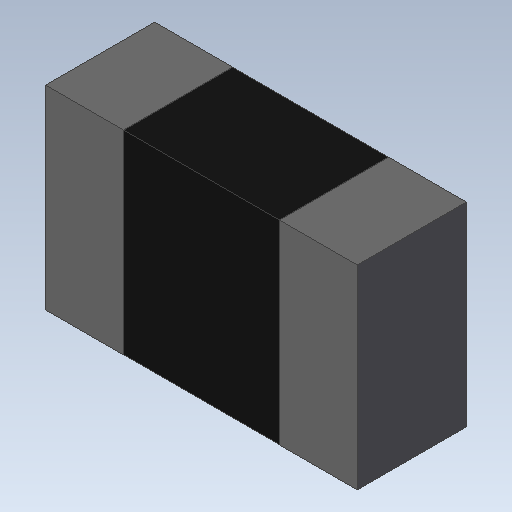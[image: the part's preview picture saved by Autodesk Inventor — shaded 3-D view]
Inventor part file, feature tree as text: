
AUTODESK INVENTOR PART (.ipt)
format: ipt  version: 2020 (Build 240168000, 168)  size: 89,600 bytes
history: imported  units: in
note: dims shown in document units (in); Inventor stores cm internally (conversion verified against a paired STEP export)
features: imported_body x1
ambient origin geometry x8: Origin, YZ Plane, XZ Plane, XY Plane, X Axis, Y Axis, Z Axis, Center Point
bodies: Solid1 (imported_parasolid), Body2 (imported_parasolid)
feature tree (1):
  imported_body  NMx_Import_Brep_tag  [imported B-rep: ~14 faces, bbox_mm=[2.0, 1.25, 0.7]]
